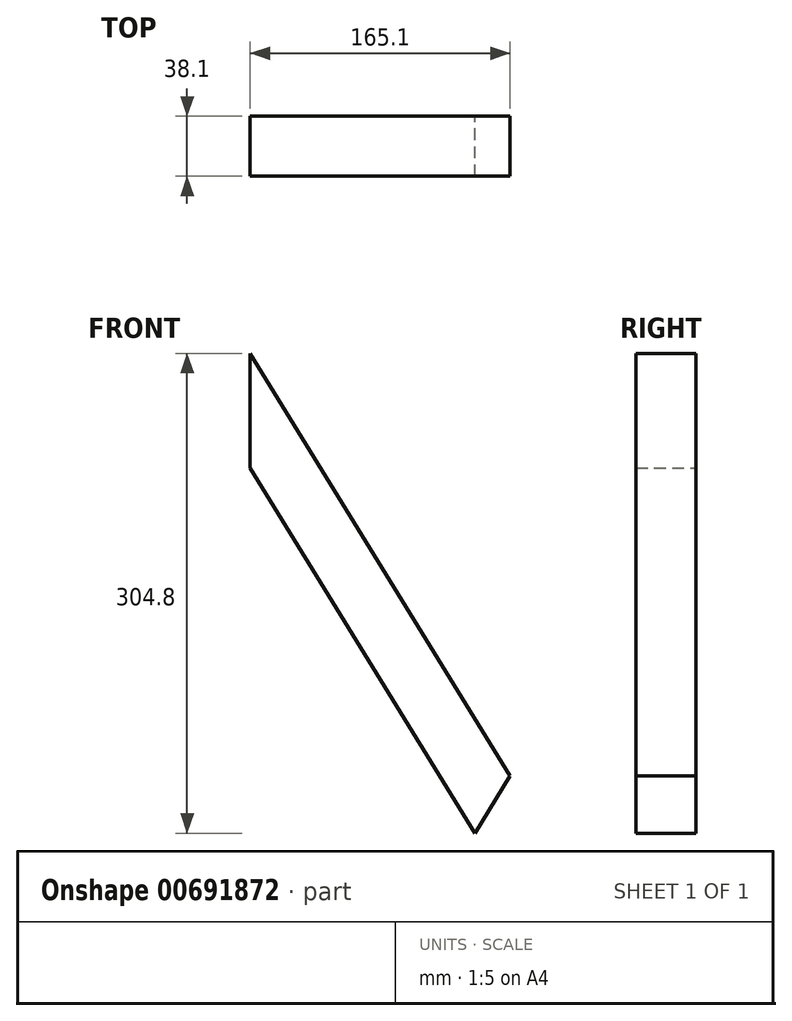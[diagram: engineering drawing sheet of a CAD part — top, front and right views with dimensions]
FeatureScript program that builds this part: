
annotation { "Feature Type Name" : "Feature", "Feature Type Description" : "" }
export const myFeature = defineFeature(function(context is Context, id is Id, definition is map)
    precondition{}
    {
        {
            var Q0;
            Q0=qCreatedBy(makeId("Front.planeOp"),FACE);
            var sketch = newSketch(context, id + "F0", { "sketchPlane" : qUnion([Q0])});
            skLineSegment(sketch, "E0.bottom", {"start": v(0, 0) * mm, "end": v(330.2, 0) * mm, "construction": true});
            skLineSegment(sketch, "E0.top", {"start": v(0, 622.3) * mm, "end": v(330.2, 622.3) * mm, "construction": true});
            skLineSegment(sketch, "E0.left", {"start": v(0, 0) * mm, "end": v(0, 622.3) * mm, "construction": true});
            skLineSegment(sketch, "E0.right", {"start": v(330.2, 0) * mm, "end": v(330.2, 622.3) * mm, "construction": true});
            skLineSegment(sketch, "E1", {"start": v(0, 615.95) * mm, "end": v(330.2, 615.95) * mm, "construction": true});
            skLineSegment(sketch, "E2", {"start": v(0, 6.35) * mm, "end": v(330.2, 6.35) * mm, "construction": true});
            skLineSegment(sketch, "E3", {"start": v(0, 543.22) * mm, "end": v(330.2, 543.22) * mm, "construction": true});
            skLineSegment(sketch, "E4", {"start": v(0, 79.08) * mm, "end": v(330.2, 79.08) * mm, "construction": true});
            skLineSegment(sketch, "E5", {"start": v(0, 543.22) * mm, "end": v(142.74, 311.15) * mm});
            skLineSegment(sketch, "E6", {"start": v(330.2, 79.08) * mm, "end": v(330.2, 6.35) * mm});
            skLineSegment(sketch, "E7", {"start": v(0, 615.95) * mm, "end": v(0, 543.22) * mm});
            skLineSegment(sketch, "E8", {"start": v(330.2, 543.22) * mm, "end": v(0, 6.35) * mm, "construction": true});
            skLineSegment(sketch, "E9", {"start": v(0, 79.08) * mm, "end": v(330.2, 615.95) * mm, "construction": true});
            skLineSegment(sketch, "E10", {"start": v(165.1, 347.51) * mm, "end": v(142.74, 311.15) * mm});
            skLineSegment(sketch, "E11", {"start": v(165.1, 274.79) * mm, "end": v(187.46, 311.15) * mm});
            skLineSegment(sketch, "E12.trimOffspring", {"start": v(165.1, 347.51) * mm, "end": v(0, 615.95) * mm});
            skLineSegment(sketch, "E13", {"start": v(0, 615.95) * mm, "end": v(330.2, 79.08) * mm, "construction": true});
            skLineSegment(sketch, "E14", {"start": v(0, 543.22) * mm, "end": v(330.2, 6.35) * mm, "construction": true});
            skSolve(sketch);
        }
        {
            var Q0;
            Q0=makeQuery(id+"F0.imprint","IMPRINT",FACE,{"disambiguationData":[TD([[makeQuery(id+"F0.imprint","IMPRINT",EDGE,{"derivedFrom":sQuery(id+"F0.wireOp",EDGE,"E5")}),1.0]])]});
            extrude(context, id + "F1", {"entities" : qUnion([Q0]), "depth" : 38.1 * mm, "offsetDistance" : 25.4 * mm});
        }
    });
